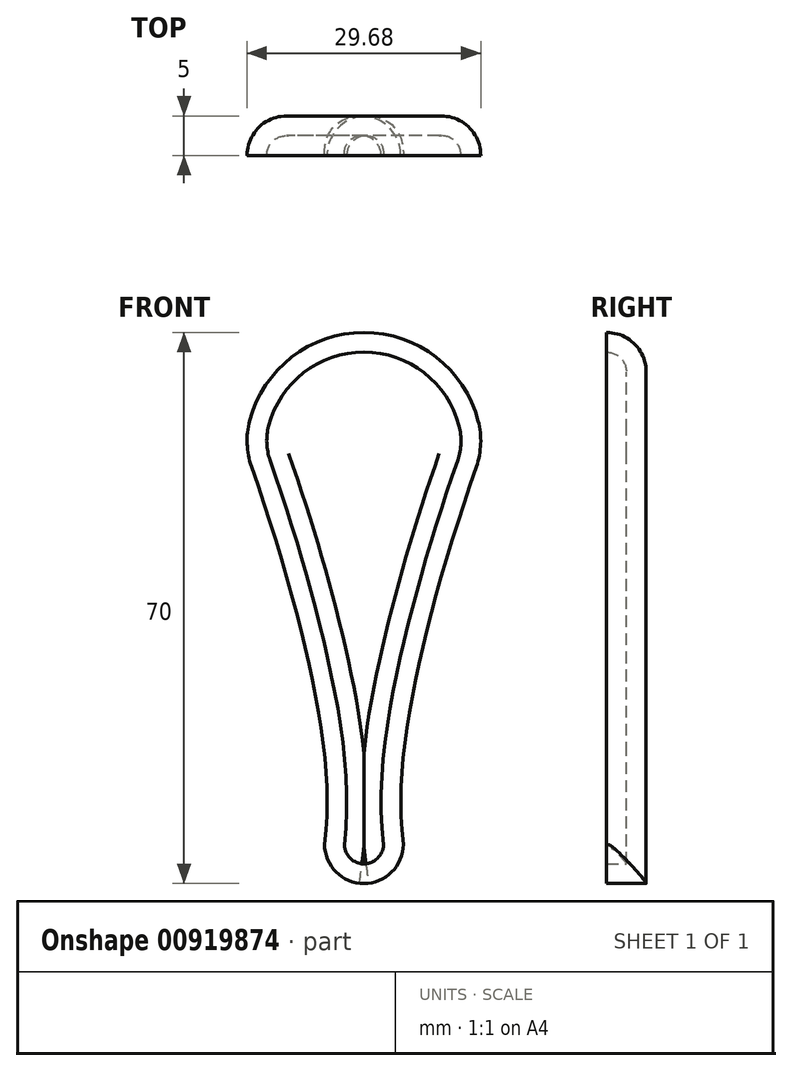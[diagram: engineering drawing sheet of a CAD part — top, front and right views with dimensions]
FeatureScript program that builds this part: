
annotation { "Feature Type Name" : "Feature", "Feature Type Description" : "" }
export const myFeature = defineFeature(function(context is Context, id is Id, definition is map)
    precondition{}
    {
        {
            var Q0;
            Q0=qCreatedBy(makeId("Front.planeOp"),FACE);
            var sketch = newSketch(context, id + "F0", { "sketchPlane" : qUnion([Q0])});
            skLineSegment(sketch, "E0", {"start": v(-49.78, 0) * mm, "end": v(50.22, 0) * mm, "construction": true});
            skLineSegment(sketch, "E1", {"start": v(0, 42.64) * mm, "end": v(0, -57.36) * mm, "construction": true});
            skArc(sketch, "E2", {"start": v(14.52, 3.77) * mm, "mid": v(0, 15) * mm, "end": v(-14.52, 3.77) * mm});
            skArc(sketch, "E3", {"start": v(-5, -50) * mm, "mid": v(0, -55) * mm, "end": v(5, -50) * mm});
            skLineSegment(sketch, "E4", {"start": v(-15.22, -50) * mm, "end": v(15.03, -50) * mm, "construction": true});
            skFitSpline(sketch, "E5", {"points": [v(-15, 0) * mm, v(-6.39, -30) * mm, v(-5, -50) * mm], "startDerivative": vector(20.2, -56.53) * mm, "endDerivative": vector(-5.14, -42.97) * mm});
            skFitSpline(sketch, "E6.MirrorCS", {"points": [v(15, 0) * mm, v(6.39, -30) * mm, v(5, -50) * mm], "startDerivative": vector(-20.2, -56.53) * mm, "endDerivative": vector(5.14, -42.97) * mm});
            skArc(sketch, "E7.filletArc", {"start": v(-14.52, 3.77) * mm, "mid": v(-14.83, 0.85) * mm, "end": v(-14.28, -2.04) * mm});
            skArc(sketch, "E8.MirrorCS", {"start": v(14.52, 3.77) * mm, "mid": v(14.83, 0.85) * mm, "end": v(14.28, -2.04) * mm});
            skSolve(sketch);
        }
        {
            var Q0;
            Q0 = qSketchRegion(id + "F0", true);
            extrude(context, id + "F1", {"entities" : qUnion([Q0]), "depth" : 5 * mm, "offsetDistance" : 25 * mm});
        }
        {
            var Q0;
            Q0=makeQuery(id+"F1.opExtrude","CAP_EDGE",EDGE,{"disambiguationData":[OSD([sQuery(id+"F0.wireOp",EDGE,"E2")])],"isStart":true});
            fillet(context, id + "F2", {"entities" : qUnion([Q0]), "radius" : 5 * mm, "tangentPropagation" : true, "allowEdgeOverflow" : false});
        }
        {
            var Q0;
            Q0=makeQuery(id+"F1.opExtrude","CAP_FACE",FACE,{"disambiguationData":[OSD([sQuery(id+"F0.wireOp",EDGE,"E2"),sQuery(id+"F0.wireOp",EDGE,"E3"),sQuery(id+"F0.wireOp",EDGE,"E5"),sQuery(id+"F0.wireOp",EDGE,"E6.MirrorCS"),sQuery(id+"F0.wireOp",EDGE,"E7.filletArc"),sQuery(id+"F0.wireOp",EDGE,"E8.MirrorCS")])],"isStart":false});
            shell(context, id + "F3", {"entities" : qUnion([Q0]), "thickness" : 2.5 * mm});
        }
    });
